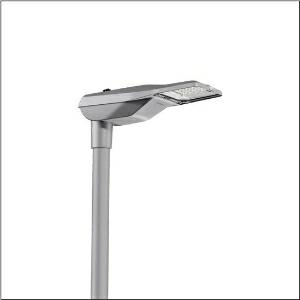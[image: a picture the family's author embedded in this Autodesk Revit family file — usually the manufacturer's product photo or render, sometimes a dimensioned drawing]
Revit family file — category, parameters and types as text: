
# Revit family: streetlight_sl_21_micro___stw1_0a_5xe1e43s08db_ea06
name_source: partatom
category: Lighting Fixtures
units: mm (PartAtom-declared; Revit-internal decimal feet)

## family parameters
Cut with Voids When Loaded = No
Host = Face
Light Source = No
Part Type = Normal
Room Calculation Point = No
Round Connector Dimension = Use Diameter
Shared = No

## types (1)
- --- (1 x LED, 5320 lm, 39.1 W, 4000K)
    Apparent Load = 39 VA
    CIE Flux Codes = 38 75 98 100 100
    Color Rendering = 70
    Color Temperature = 4000K
    Default Elevation = 1800 mm
    Description = Streetlight SL 21 micro, mast luminaire, primary light control with lens, of PMMA, primary optical cover: cover, of toughened safety glass, transparent, light distribution: STW1.0a, light emission: direct distribution, primary light characteristic: asymmetric, installation type: side-entry, post-top, LED, High Power LED, rated luminous flux: 5.320lm, luminous efficacy: 136lm/W, light colour: 740, colour temperature: 4000K, control gear: D4i, control: flexible luminous flux parameterisation, time-dependent luminous flux control, constant luminous flux control, overheat protection, pre-setting: logarithmic dimming characteristic, mains connection: 220..240V, AC, 50/60Hz, start of lifetime: 39W, end of service life: 41W, reduction: 18W, luminaire housing, of diecast aluminium, powder-coated, SITECO metallic grey (DB 702S), corrosivity category C5 high according to DIN EN ISO 12944, please order mast flange separately, inclination adjustable: 0°, 5°, 10°, 15°, sealing non-destructively replaceable, multi-level sealing system, length: 528mm, width: 235mm, height: 110mm, mast flange for spigot size: 42mm (side-entry): 5XC10008XM4, 60/48mm (side-entry/post-top): 5XC10108XM2, 76/60mm (side-entry/post-top): 5XC10108XM1, Smart Interface above, protection rating (complete): IP66, insulation class (complete): insulation class II (safety insulation), certification: CE, ENEC, ENEC+, VDE, impact resistance: IK10, permissible operating ambient temperature for outdoor applications: -40..+50°C, standard-compliant lighting for roads and squares, packaging unit: 1 piece

Light Distribution: STW1.0a
    Height = 110 mm
    Lamp = 1 x LED
    Lamp Light Flux = 5320 lm
    Lamp Power = 39.1 W
    Lamp count = 1
    Length = 528 mm
    Luminous efficacy = 136 lm/W
    Manufacturer = Siteco
    ModVariant = No
    Model = 5XE1E43S08DB
    Number of Poles = 1
    OnlyDefault = Yes
    Power Factor = 1
    Product Name = Streetlight SL 21 micro | STW1.0a
    Product group = mast luminaire | pylon top
    ProductGroupID = 6100
    Protection Class = Protection class II
    Protection Degree = IP 66
    RLX_Detail_Level = 1
    RLX_Emergency_Light_Flux = 0 lm
    RLX_Emergency_Type = 0
    RLX_Emergency_Type_DB = No
    RlxData = <blob elided: 98585 chars, md5=a1cf3ecd>
    Socket = socket
    Standby Power = 0 W
    System Light Flux = 5320 lm
    System Power = 39 W
    Type Comments = factory setting: luminous flux: 100 % | dim-lin: 254 | 765 mA
    Type Image = l_1277292.jpg
    URL = http://relux.com
    VarID = @adj_154801
    Voltage = 0 V
    Weight = 0.00 kg
    Width = 235 mm

## geometry (parser evidence)
native form markers: Blend x4, Sweep x10
no freeform markers — native parametric forms only
